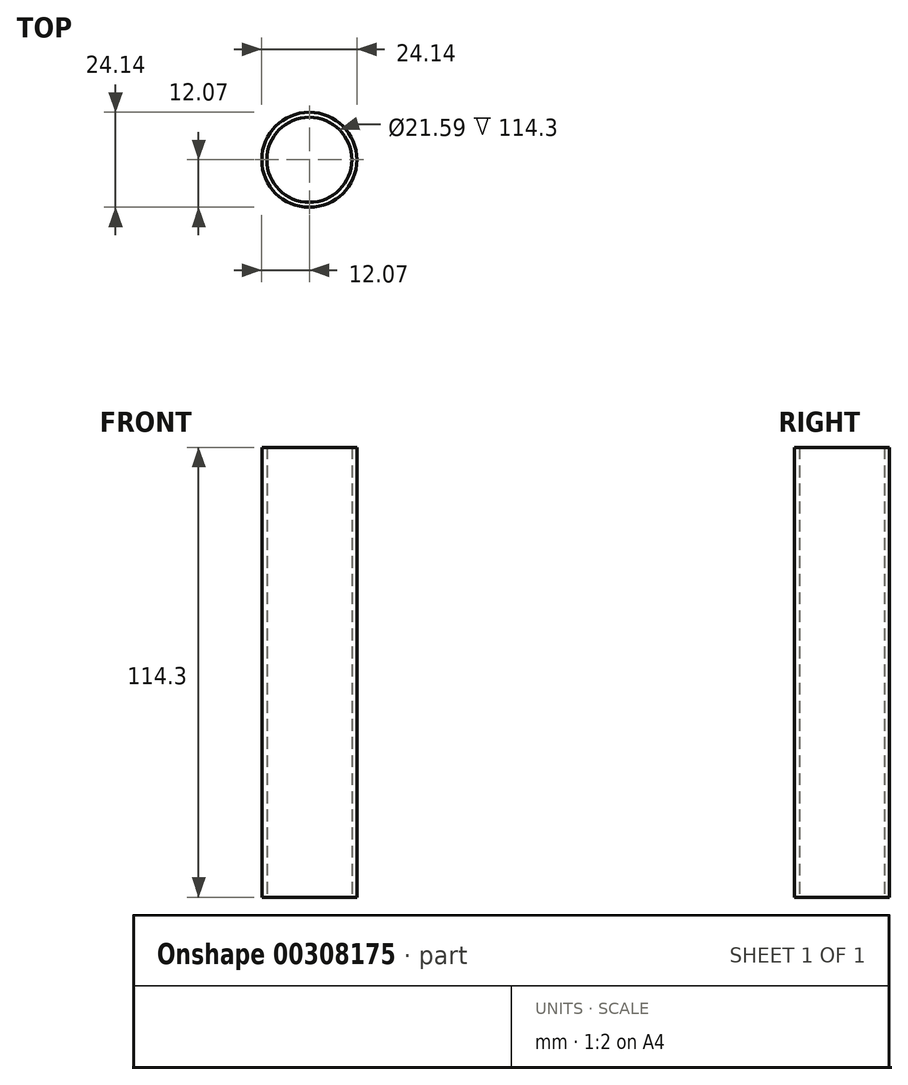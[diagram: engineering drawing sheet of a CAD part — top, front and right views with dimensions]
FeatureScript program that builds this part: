
annotation { "Feature Type Name" : "Feature", "Feature Type Description" : "" }
export const myFeature = defineFeature(function(context is Context, id is Id, definition is map)
    precondition{}
    {
        {
            var Q0;
            Q0=qCreatedBy(makeId("Top.planeOp"),FACE);
            var sketch = newSketch(context, id + "F0", { "sketchPlane" : qUnion([Q0])});
            skCircle(sketch, "E0", {"center": v(0, 0) * mm, "radius": 12.07 * mm});
            skCircle(sketch, "E1", {"center": v(0, 0) * mm, "radius": 10.8 * mm});
            skSolve(sketch);
        }
        {
            var Q0;
            Q0=makeQuery(id+"F0.imprint","IMPRINT",FACE,{"disambiguationData":[TD([[makeQuery(id+"F0.imprint","IMPRINT",EDGE,{"derivedFrom":sQuery(id+"F0.wireOp",EDGE,"E0")}),1.0]])]});
            extrude(context, id + "F1", {"entities" : qUnion([Q0]), "depth" : 114.3 * mm});
        }
    });
